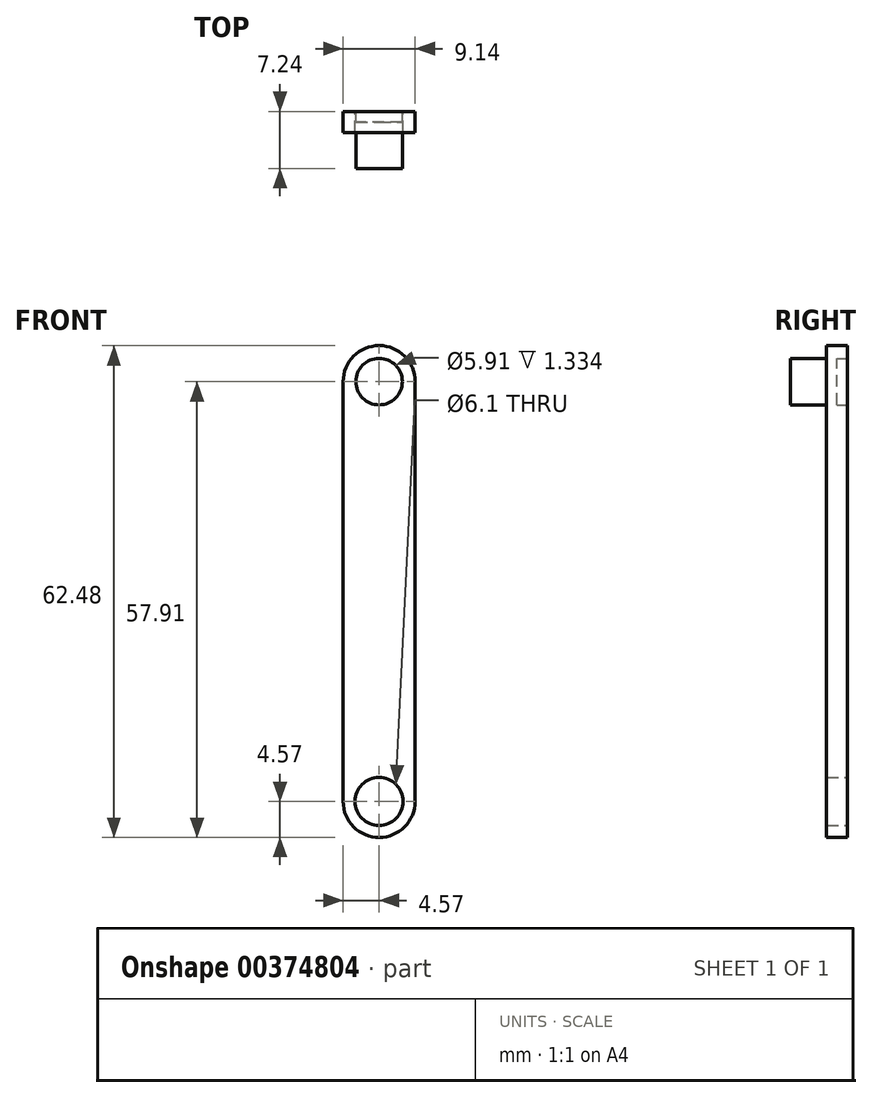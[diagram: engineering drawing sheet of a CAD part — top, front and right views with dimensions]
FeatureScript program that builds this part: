
annotation { "Feature Type Name" : "Feature", "Feature Type Description" : "" }
export const myFeature = defineFeature(function(context is Context, id is Id, definition is map)
    precondition{}
    {
        {
            var Q0;
            Q0=qCreatedBy(makeId("Front.planeOp"),FACE);
            var sketch = newSketch(context, id + "F0", { "sketchPlane" : qUnion([Q0])});
            skLineSegment(sketch, "E0", {"start": v(-0.6, 7.11) * mm, "end": v(-0.6, 0) * mm});
            skLineSegment(sketch, "E1", {"start": v(0.6, 7.11) * mm, "end": v(0.6, 0) * mm});
            skArc(sketch, "E2", {"start": v(0, 7.72) * mm, "mid": v(-0.43, 7.54) * mm, "end": v(-0.6, 7.11) * mm});
            skArc(sketch, "E3", {"start": v(0.6, 7.11) * mm, "mid": v(0.43, 7.54) * mm, "end": v(0, 7.72) * mm});
            skArc(sketch, "E4", {"start": v(-0.6, 0) * mm, "mid": v(-0.43, -0.43) * mm, "end": v(0, -0.6) * mm});
            skArc(sketch, "E5", {"start": v(0, -0.6) * mm, "mid": v(0.43, -0.43) * mm, "end": v(0.6, 0) * mm});
            skCircle(sketch, "E6", {"center": v(0, 7.11) * mm, "radius": 0.4 * mm});
            skCircle(sketch, "E7", {"center": v(0, 0) * mm, "radius": 0.4 * mm});
            skSolve(sketch);
        }
        {
            var Q0;
            Q0=makeQuery(id+"F0.imprint","IMPRINT",FACE,{"disambiguationData":[TD([[makeQuery(id+"F0.imprint","IMPRINT",EDGE,{"derivedFrom":sQuery(id+"F0.wireOp",EDGE,"E0")}),1.0]])]});
            extrude(context, id + "F1", {"entities" : qUnion([Q0]), "endBound" : BoundingType.SYMMETRIC, "depth" : 0.36 * mm, "offsetDistance" : 25.4 * mm});
        }
        {
            var Q0;
            Q0=makeQuery(id+"F0.imprint","IMPRINT",FACE,{"disambiguationData":[TD([[makeQuery(id+"F0.imprint","IMPRINT",EDGE,{"derivedFrom":sQuery(id+"F0.wireOp",EDGE,"E6")}),1.0]])]});
            extrude(context, id + "F2", {"entities" : qUnion([Q0]), "operationType" : NewBodyOperationType.ADD, "depth" : 0.79 * mm, "offsetDistance" : 25.4 * mm});
        }
        {
            var Q0;
            Q0=makeQuery(id+"F1.opExtrude","SWEPT_BODY",BODY,{"disambiguationData":[OSD([sQuery(id+"F0.wireOp",EDGE,"E0"),sQuery(id+"F0.wireOp",EDGE,"E1"),sQuery(id+"F0.wireOp",EDGE,"E2"),sQuery(id+"F0.wireOp",EDGE,"E3"),sQuery(id+"F0.wireOp",EDGE,"E4"),sQuery(id+"F0.wireOp",EDGE,"E5"),sQuery(id+"F0.wireOp",EDGE,"E6"),sQuery(id+"F0.wireOp",EDGE,"E7")])]});
            var Q1;
            Q1=qCreatedBy(makeId("Origin.pointOp"),VERTEX);
            transform(context, id + "F3", {"entities" : qUnion([Q0]), "transformType" : TransformType.SCALE_UNIFORMLY, "scale" : 7.5, "scalePoint" : qUnion([Q1]), "makeCopy" : false});
        }
    });
